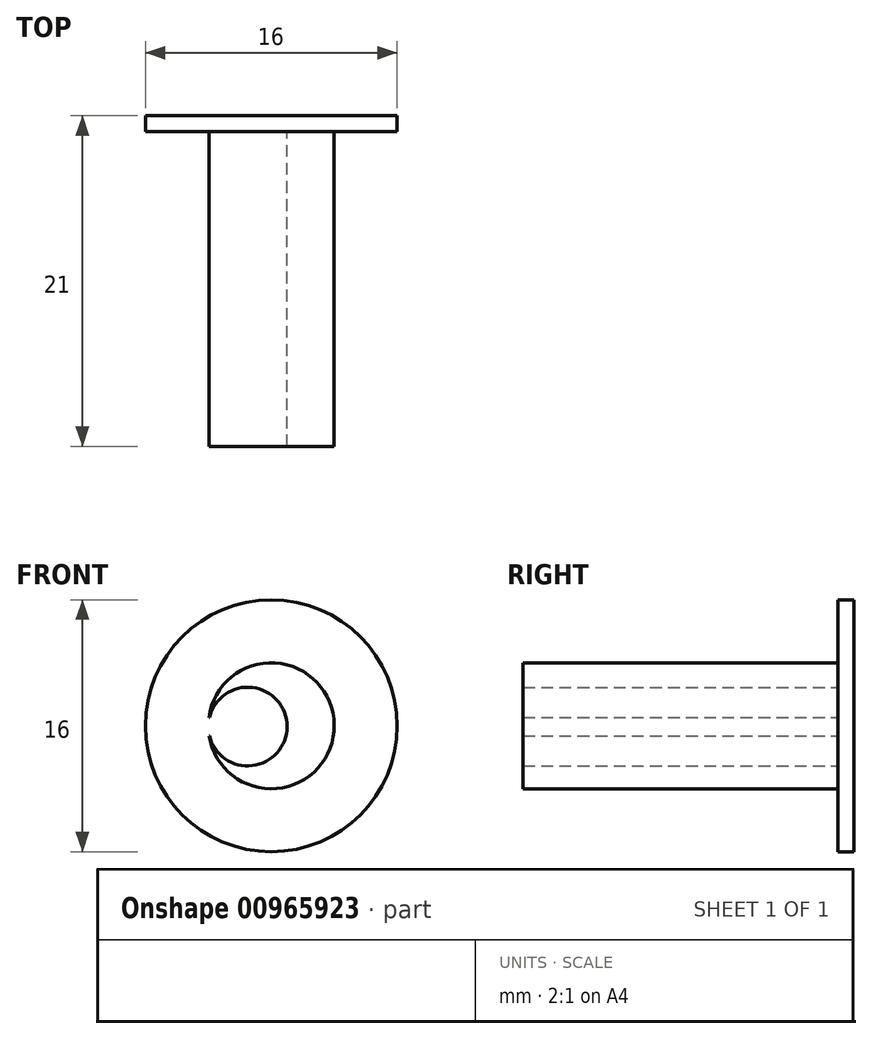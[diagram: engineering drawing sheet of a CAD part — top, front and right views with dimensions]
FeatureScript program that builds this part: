
annotation { "Feature Type Name" : "Feature", "Feature Type Description" : "" }
export const myFeature = defineFeature(function(context is Context, id is Id, definition is map)
    precondition{}
    {
        {
            var Q0;
            Q0=qCreatedBy(makeId("Front.planeOp"),FACE);
            var sketch = newSketch(context, id + "F0", { "sketchPlane" : qUnion([Q0])});
            skArc(sketch, "E0", {"start": v(-3.95, -0.64) * mm, "mid": v(4, 0.05) * mm, "end": v(-3.96, 0.54) * mm});
            skArc(sketch, "E1", {"start": v(-3.93, -0.64) * mm, "mid": v(1, -0.05) * mm, "end": v(-3.93, 0.54) * mm});
            skLineSegment(sketch, "E2.bottom", {"start": v(-3.95, -0.64) * mm, "end": v(-3.93, -0.64) * mm});
            skLineSegment(sketch, "E2.top", {"start": v(-3.96, 0.54) * mm, "end": v(-3.93, 0.54) * mm});
            skPoint(sketch, "E3.trimOffspring.end.orphan", {"position": v(1.1, 0.54) * mm});
            skPoint(sketch, "E4.trimOffspring.end.orphan", {"position": v(1.1, -0.64) * mm});
            skPoint(sketch, "E5.orphan", {"position": v(-4.1, 0.54) * mm});
            skPoint(sketch, "E6.orphan", {"position": v(-4.1, -0.64) * mm});
            skSolve(sketch);
        }
        {
            var Q0;
            Q0=makeQuery(id+"F0.imprint","IMPRINT",FACE,{"disambiguationData":[TD([[makeQuery(id+"F0.imprint","IMPRINT",EDGE,{"derivedFrom":sQuery(id+"F0.wireOp",EDGE,"E0")}),1.0]])]});
            extrude(context, id + "F1", {"entities" : qUnion([Q0]), "depth" : 21 * mm, "offsetDistance" : 25 * mm});
        }
        {
            var Q0;
            Q0=makeQuery(id+"F1.opExtrude","CAP_FACE",FACE,{"disambiguationData":[OSD([sQuery(id+"F0.wireOp",EDGE,"E0"),sQuery(id+"F0.wireOp",EDGE,"E1")])],"isStart":true});
            var sketch = newSketch(context, id + "F2", { "sketchPlane" : qUnion([Q0])});
            skCircle(sketch, "E7", {"center": v(0, 0) * mm, "radius": 8 * mm});
            skCircle(sketch, "E8.0", {"center": v(1.5, -0.05) * mm, "radius": 2.5 * mm});
            skSolve(sketch);
        }
        {
            var Q0;
            Q0=makeQuery(id+"F2.imprint","IMPRINT",FACE,{"disambiguationData":[TD([[makeQuery(id+"F2.imprint","IMPRINT",EDGE,{"derivedFrom":sQuery(id+"F2.wireOp",EDGE,"E7")}),1.0]])]});
            var Q1;
            Q1=makeQuery(id+"F2.imprint","IMPRINT",FACE,{"disambiguationData":[TD([[makeQuery(id+"F2.imprint","IMPRINT",EDGE,{"derivedFrom":sQuery(id+"F2.wireOp",EDGE,"E8.0")}),1.0]])]});
            extrude(context, id + "F3", {"entities" : qUnion([Q0, Q1]), "operationType" : NewBodyOperationType.ADD, "oppositeDirection" : true, "depth" : 1 * mm, "offsetDistance" : 25 * mm});
        }
    });
